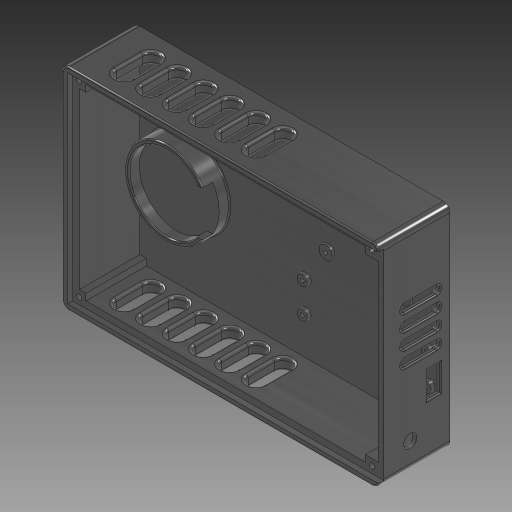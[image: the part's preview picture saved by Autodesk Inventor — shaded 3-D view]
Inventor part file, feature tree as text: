
AUTODESK INVENTOR PART (.ipt)
format: ipt  version: 2023 (Build 270158000, 158)  size: 1,201,152 bytes
history: native  units: mm
features: extrude x10, sketch x10, fillet x3, other x1, mirror x1
ambient origin geometry x8: Origin, YZ Plane, XZ Plane, XY Plane, X Axis, Y Axis, Z Axis, Center Point
bodies: Body1 (feature_tree)
feature tree (25):
  other  "Těleso1"
  extrude  "Vysunutí1"  Depth=120.0mm
  extrude  "Vysunutí2"  Depth=80.0mm
  extrude  "micro usb hole"  Depth=2.0mm TaperAngle=0.0deg
  extrude  "rpi holder"  Depth=116.0mm
  extrude  "rgb led hole"  Depth=25.0mm TaperAngle=0.0deg
  extrude  "ULN2003 holder"  Depth=3.5mm
  extrude  "Vysunutí10"  Depth=5.0mm
  extrude  "Vysunutí11"  Depth=10.0mm
  extrude  "Vysunutí12"  Depth=5.0mm TaperAngle=0.0deg
  extrude  "Vysunutí14"  Depth=3.8mm
  fillet  "Zaoblení1"  Radius=3.8mm
  fillet  "Zaoblení2"  Radius=11.4mm
  mirror  "Zrcadlit2"
  fillet  "Zaoblení3"  Radius=3.8mm
  sketch  "Náčrt1"
  sketch  "Náčrt2"
  sketch  "Náčrt3"
  sketch  "Náčrt4"
  sketch  "Náčrt6"
  sketch  "Náčrt7"
  sketch  "Náčrt10"
  sketch  "Náčrt11"
  sketch  "Náčrt12"
  sketch  "Náčrt15"
